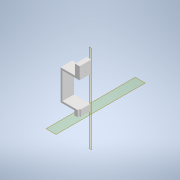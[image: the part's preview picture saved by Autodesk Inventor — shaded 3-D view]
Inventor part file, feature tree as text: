
AUTODESK INVENTOR PART (.ipt)
format: ipt  version: 2020 (Build 240168000, 168)  size: 190,976 bytes
history: native  units: mm
features: reference x19, other x11, sketch x5, projected_geometry x4, extrude x3, hole x2
ambient origin geometry x8: Origin, YZ Plane, XZ Plane, XY Plane, X Axis, Y Axis, Z Axis, Center Point
bodies: Body1 (feature_tree)
feature tree (44):
  other  "솔리드1"
  other  "작업 평면1"
  extrude  "돌출1"  Depth=67.0mm TaperAngle=0.0deg
  other  "작업 평면2"
  extrude  "돌출2"  Depth=67.0mm TaperAngle=0.0deg
  hole  "구멍1"  [1 undecoded]
  hole  "구멍2"  [1 undecoded]
  extrude  "돌출4"  Depth=10.0mm
  sketch  "스케치1"
  reference  "참조1"
  reference  "참조2"
  reference  "참조3"
  reference  "참조4"
  reference  "참조5"
  reference  "참조6"
  reference  "참조7"
  reference  "참조8"
  reference  "참조9"
  reference  "참조10"
  reference  "참조11"
  reference  "참조12"
  reference  "참조13"
  reference  "참조14"
  sketch  "스케치2"
  reference  "참조15"
  projected_geometry  "투영된 루프1"
  reference  "참조16"
  sketch  "스케치6"
  reference  "참조23"
  reference  "참조24"
  projected_geometry  "투영된 루프3"
  projected_geometry  "투영된 루프4"
  sketch  "스케치9"
  reference  "참조25"
  sketch  "스케치10"
  projected_geometry  "투영된 루프5"
  parser-record x1  (decoder bookkeeping rows leaked as tree rows — omitted from the tree; the rows remain in map.json)
  other  "v6.iam"
  other  "AL_profile_final:1"
  other  "bumper_final_6:2"
  other  "Axel_arch_final_v4:2"
  other  "Axel_crossbar_final_v2:2"
  other  "cross_AL_profile:2"
  other  "STM_Rear:1"
note: 2 required parameter values undecoded (feature->parameter linkage not recoverable at this tier; creation-order binding heuristic only, values carry confidence <= 0.55)
note: 1 file-system path scrubbed to <path> (originals preserved in map.json)
